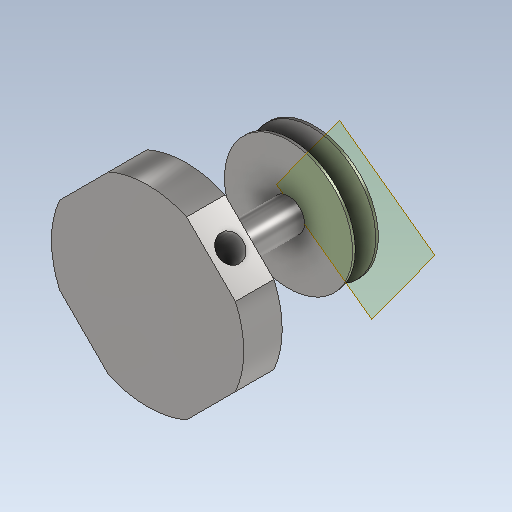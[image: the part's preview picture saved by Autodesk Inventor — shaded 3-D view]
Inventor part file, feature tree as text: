
AUTODESK INVENTOR PART (.ipt)
format: ipt  version: 2021 (Build 250183000, 183)  size: 189,952 bytes
history: native  units: mm
features: extrude x7, sketch x6, other x4, chamfer x2, reference x1, projected_geometry x1
ambient origin geometry x8: Origin, YZ Plane, XZ Plane, XY Plane, X Axis, Y Axis, Z Axis, Center Point
bodies: Body1 (feature_tree)
feature tree (21):
  other  "Bryła1"
  other  "Płaszczyzna konstrukcyjna1"
  extrude  "Wyciągnięcie proste1"  Depth=25.0mm
  extrude  "Wyciągnięcie proste2"  Depth=20.0mm TaperAngle=0.0deg
  chamfer  "Faza1"  Distance=100.0mm
  extrude  "Wyciągnięcie proste3"  Depth=10.0mm TaperAngle=0.0deg
  chamfer  "Faza2"  Distance=37.0mm Angle=45.0deg
  extrude  "Wyciągnięcie proste4"  Depth=100.0mm
  extrude  "Wyciągnięcie proste5"  Depth=10.0mm TaperAngle=0.0deg
  extrude  "Wyciągnięcie proste6"  Depth=37.0mm TaperAngle=45.0deg
  extrude  "Wyciągnięcie proste7"  Depth=150.0mm
  reference  "Odniesienie1"
  sketch  "Szkic2"
  sketch  "Szkic3"
  sketch  "Szkic4"
  sketch  "Szkic5"
  sketch  "Szkic6"
  sketch  "Szkic7"
  projected_geometry  "Pętla rzutowana1"
  other  "cw12model.iam"
  other  "jakis_modulxD:1"
